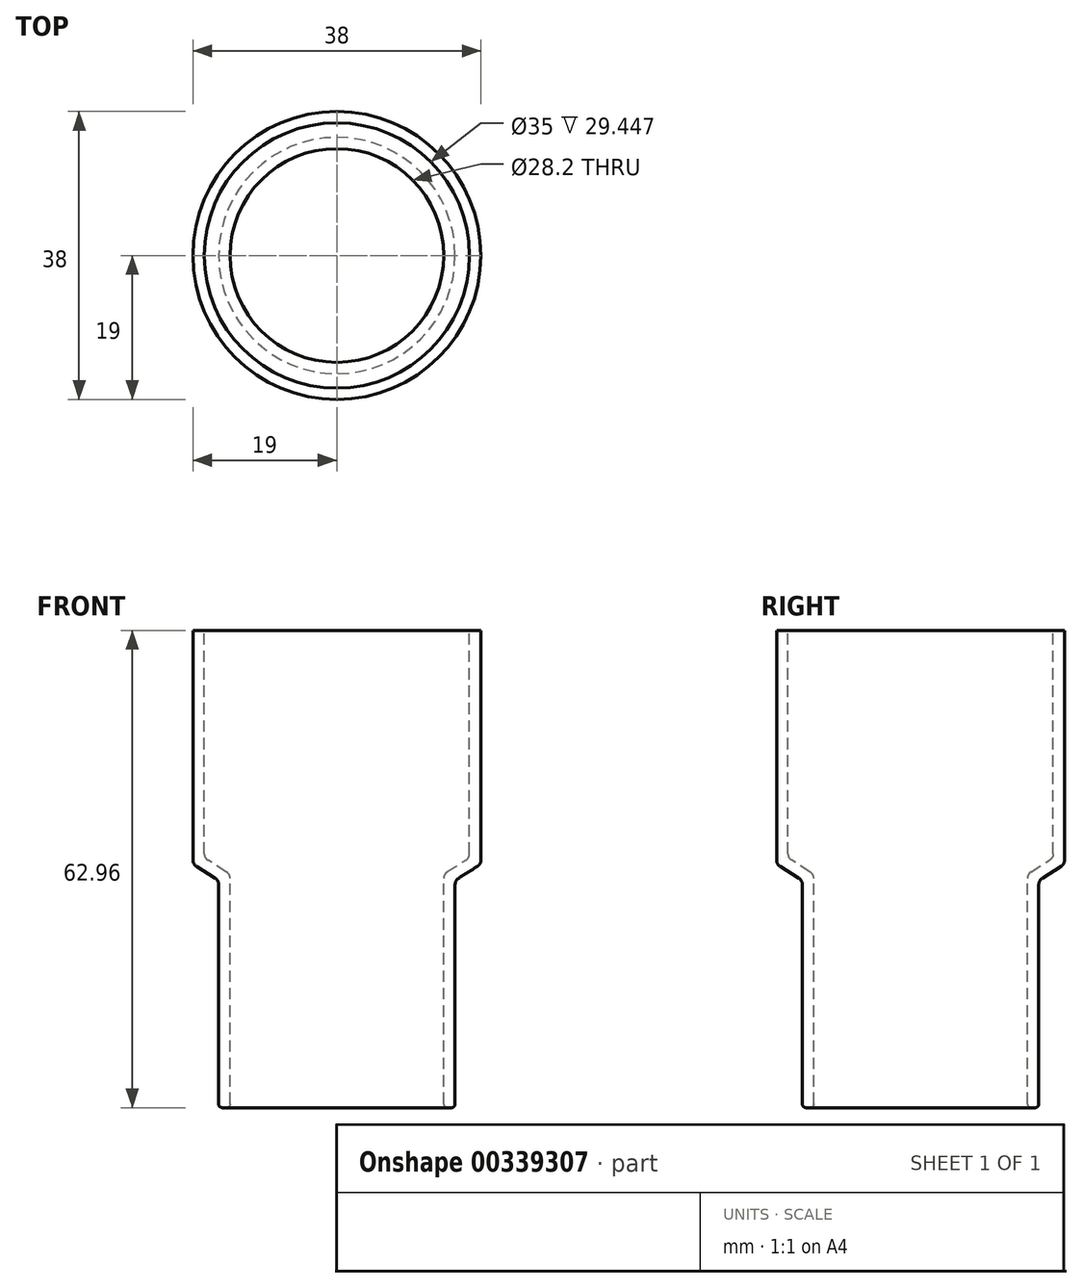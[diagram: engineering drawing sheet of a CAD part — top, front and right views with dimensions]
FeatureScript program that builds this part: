
annotation { "Feature Type Name" : "Feature", "Feature Type Description" : "" }
export const myFeature = defineFeature(function(context is Context, id is Id, definition is map)
    precondition{}
    {
        {
            var Q0;
            Q0=qCreatedBy(makeId("Front.planeOp"),FACE);
            var sketch = newSketch(context, id + "F0", { "sketchPlane" : qUnion([Q0])});
            skLineSegment(sketch, "E0", {"start": v(-17.5, 30) * mm, "end": v(-17.5, 0) * mm});
            skLineSegment(sketch, "E1", {"start": v(-14.1, -2.13) * mm, "end": v(-14.1, -32.96) * mm});
            skLineSegment(sketch, "E2", {"start": v(-14.1, -32.96) * mm, "end": v(-15.6, -32.96) * mm});
            skLineSegment(sketch, "E3", {"start": v(-19, 30) * mm, "end": v(-17.5, 30) * mm});
            skLineSegment(sketch, "E4", {"start": v(-17.5, 0) * mm, "end": v(-14.1, -2.13) * mm});
            skLineSegment(sketch, "E5", {"start": v(-19, 30) * mm, "end": v(-19, -0.83) * mm});
            skLineSegment(sketch, "E6", {"start": v(-19, -0.83) * mm, "end": v(-15.6, -2.96) * mm});
            skLineSegment(sketch, "E7", {"start": v(-15.6, -2.96) * mm, "end": v(-15.6, -32.96) * mm});
            skLineSegment(sketch, "E8", {"start": v(0, 53.79) * mm, "end": v(0, -44.33) * mm});
            skSolve(sketch);
        }
        {
            var Q0;
            Q0=makeQuery(id+"F0.imprint","IMPRINT",FACE,{"disambiguationData":[TD([[makeQuery(id+"F0.imprint","IMPRINT",EDGE,{"derivedFrom":sQuery(id+"F0.wireOp",EDGE,"E0")}),-1.0]])]});
            var Q1;
            Q1=sQuery(id+"F0.wireOp",EDGE,"E8");
            revolve(context, id + "F1", {"entities" : qUnion([Q0]), "axis" : qUnion([Q1]), "revolveType" : RevolveType.FULL});
        }
        {
            var Q0;
            Q0=makeQuery(id+"F1.opRevolve","SWEPT_EDGE",EDGE,{"disambiguationData":[OSD([sQuery(id+"F0.wireOp",EDGE,"E2"),sQuery(id+"F0.wireOp",EDGE,"E7")])]});
            var Q1;
            Q1=makeQuery(id+"F1.opRevolve","SWEPT_EDGE",EDGE,{"disambiguationData":[OSD([sQuery(id+"F0.wireOp",EDGE,"E1"),sQuery(id+"F0.wireOp",EDGE,"E2")])]});
            fillet(context, id + "F2", {"entities" : qUnion([Q0, Q1]), "radius" : 0.5 * mm, "tangentPropagation" : true, "allowEdgeOverflow" : false});
        }
        {
            var Q0;
            Q0=makeQuery(id+"F1.opRevolve","SWEPT_EDGE",EDGE,{"disambiguationData":[OSD([sQuery(id+"F0.wireOp",EDGE,"E5"),sQuery(id+"F0.wireOp",EDGE,"E6")])]});
            var Q1;
            Q1=makeQuery(id+"F1.opRevolve","SWEPT_EDGE",EDGE,{"disambiguationData":[OSD([sQuery(id+"F0.wireOp",EDGE,"E6"),sQuery(id+"F0.wireOp",EDGE,"E7")])]});
            fillet(context, id + "F3", {"entities" : qUnion([Q0, Q1]), "radius" : 1 * mm, "tangentPropagation" : true, "allowEdgeOverflow" : false});
        }
        {
            var Q0;
            Q0=makeQuery(id+"F1.opRevolve","SWEPT_EDGE",EDGE,{"disambiguationData":[OSD([sQuery(id+"F0.wireOp",EDGE,"E1"),sQuery(id+"F0.wireOp",EDGE,"E4")])]});
            var Q1;
            Q1=makeQuery(id+"F1.opRevolve","SWEPT_EDGE",EDGE,{"disambiguationData":[OSD([sQuery(id+"F0.wireOp",EDGE,"E0"),sQuery(id+"F0.wireOp",EDGE,"E4")])]});
            fillet(context, id + "F4", {"entities" : qUnion([Q0, Q1]), "radius" : 1 * mm, "tangentPropagation" : true, "allowEdgeOverflow" : false});
        }
    });
